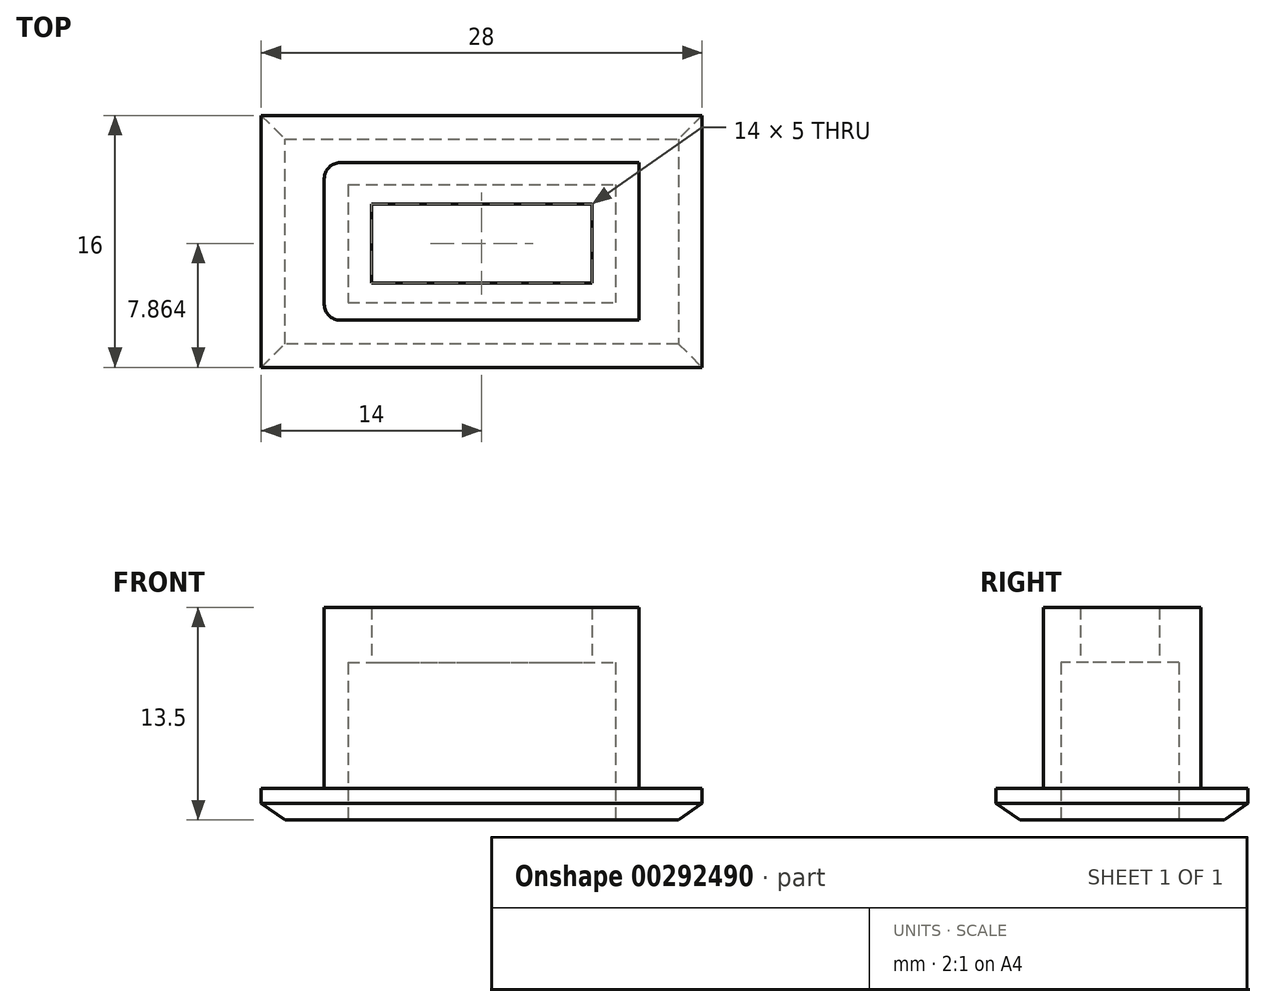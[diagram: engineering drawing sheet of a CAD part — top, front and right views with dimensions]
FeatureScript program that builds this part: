
annotation { "Feature Type Name" : "Feature", "Feature Type Description" : "" }
export const myFeature = defineFeature(function(context is Context, id is Id, definition is map)
    precondition{}
    {
        {
            var Q0;
            Q0=qCreatedBy(makeId("Front.planeOp"),FACE);
            var sketch = newSketch(context, id + "F0", { "sketchPlane" : qUnion([Q0])});
            skLineSegment(sketch, "E0.bottom", {"start": v(10, 5.75) * mm, "end": v(-10, 5.75) * mm});
            skLineSegment(sketch, "E0.top", {"start": v(10, -5.75) * mm, "end": v(-10, -5.75) * mm});
            skLineSegment(sketch, "E0.left", {"start": v(10, 5.75) * mm, "end": v(10, -5.75) * mm});
            skLineSegment(sketch, "E0.right", {"start": v(-10, 5.75) * mm, "end": v(-10, -5.75) * mm});
            skPoint(sketch, "E0.middle", {"position": v(0, 0) * mm});
            skLineSegment(sketch, "E1.bottom", {"start": v(-14, -5.75) * mm, "end": v(14, -5.75) * mm});
            skLineSegment(sketch, "E1.top", {"start": v(-14, -7.75) * mm, "end": v(14, -7.75) * mm});
            skLineSegment(sketch, "E1.left", {"start": v(-14, -5.75) * mm, "end": v(-14, -7.75) * mm});
            skLineSegment(sketch, "E1.right", {"start": v(14, -5.75) * mm, "end": v(14, -7.75) * mm});
            skSolve(sketch);
        }
        {
            var Q0;
            Q0=makeQuery(id+"F0.imprint","IMPRINT",FACE,{"disambiguationData":[TD([[makeQuery(id+"F0.imprint","IMPRINT",EDGE,{"derivedFrom":sQuery(id+"F0.wireOp",EDGE,"E0.bottom")}),1.0]])]});
            var Q1;
            Q1=makeQuery(id+"F0.imprint","IMPRINT",FACE,{"disambiguationData":[TD([[makeQuery(id+"F0.imprint","IMPRINT",EDGE,{"derivedFrom":sQuery(id+"F0.wireOp",EDGE,"E1.top")}),1.0]])]});
            extrude(context, id + "F1", {"entities" : qUnion([Q0, Q1]), "oppositeDirection" : true, "depth" : 16 * mm});
        }
        {
            var Q0;
            Q0=makeQuery(id+"F1.opExtrude","SWEPT_FACE",FACE,{"disambiguationData":[OSD([sQuery(id+"F0.wireOp",EDGE,"E0.left")])]});
            var sketch = newSketch(context, id + "F2", { "sketchPlane" : qUnion([Q0])});
            skLineSegment(sketch, "E2", {"start": v(8, 9.28) * mm, "end": v(8, -10.72) * mm, "construction": true});
            skLineSegment(sketch, "E3.bottom", {"start": v(0, 5.75) * mm, "end": v(3, 5.75) * mm});
            skLineSegment(sketch, "E3.top", {"start": v(0, -5.75) * mm, "end": v(3, -5.75) * mm});
            skLineSegment(sketch, "E3.left", {"start": v(0, 5.75) * mm, "end": v(0, -5.75) * mm});
            skLineSegment(sketch, "E3.right", {"start": v(3, 5.75) * mm, "end": v(3, -5.75) * mm});
            skLineSegment(sketch, "E4.MirrorCS", {"start": v(13, 5.75) * mm, "end": v(13, -5.75) * mm});
            skLineSegment(sketch, "E5.MirrorCS", {"start": v(16, 5.75) * mm, "end": v(13, 5.75) * mm});
            skLineSegment(sketch, "E6.MirrorCS", {"start": v(16, 5.75) * mm, "end": v(16, -5.75) * mm});
            skLineSegment(sketch, "E7.MirrorCS", {"start": v(16, -5.75) * mm, "end": v(13, -5.75) * mm});
            skSolve(sketch);
        }
        {
            var Q0;
            Q0=makeQuery(id+"F2.imprint","IMPRINT",FACE,{"disambiguationData":[TD([[makeQuery(id+"F2.imprint","IMPRINT",EDGE,{"derivedFrom":sQuery(id+"F2.wireOp",EDGE,"E3.bottom")}),1.0]])]});
            var Q1;
            Q1=makeQuery(id+"F2.imprint","IMPRINT",FACE,{"disambiguationData":[TD([[makeQuery(id+"F2.imprint","IMPRINT",EDGE,{"derivedFrom":sQuery(id+"F2.wireOp",EDGE,"E4.MirrorCS")}),1.0]])]});
            extrude(context, id + "F3", {"entities" : qUnion([Q0, Q1]), "operationType" : NewBodyOperationType.REMOVE, "oppositeDirection" : true, "depth" : 25 * mm});
        }
        {
            var Q0;
            Q0=makeQuery(id+"F1.opExtrude","SWEPT_FACE",FACE,{"disambiguationData":[OSD([sQuery(id+"F0.wireOp",EDGE,"E1.top")])]});
            var sketch = newSketch(context, id + "F4", { "sketchPlane" : qUnion([Q0])});
            skLineSegment(sketch, "E8", {"start": v(17.54, -7.86) * mm, "end": v(-16.5, -7.86) * mm, "construction": true});
            skLineSegment(sketch, "E9.bottom", {"start": v(-8.5, -11.61) * mm, "end": v(8.5, -11.61) * mm});
            skLineSegment(sketch, "E9.top", {"start": v(-8.5, -4.11) * mm, "end": v(8.5, -4.11) * mm});
            skLineSegment(sketch, "E9.left", {"start": v(-8.5, -11.61) * mm, "end": v(-8.5, -4.11) * mm});
            skLineSegment(sketch, "E9.right", {"start": v(8.5, -11.61) * mm, "end": v(8.5, -4.11) * mm});
            skPoint(sketch, "E9.middle", {"position": v(0, -7.86) * mm});
            skLineSegment(sketch, "E10.bottom", {"start": v(-7, -10.36) * mm, "end": v(7, -10.36) * mm});
            skLineSegment(sketch, "E10.top", {"start": v(-7, -5.36) * mm, "end": v(7, -5.36) * mm});
            skLineSegment(sketch, "E10.left", {"start": v(-7, -10.36) * mm, "end": v(-7, -5.36) * mm});
            skLineSegment(sketch, "E10.right", {"start": v(7, -10.36) * mm, "end": v(7, -5.36) * mm});
            skSolve(sketch);
        }
        {
            var Q0;
            Q0=makeQuery(id+"F4.imprint","IMPRINT",FACE,{"disambiguationData":[TD([[makeQuery(id+"F4.imprint","IMPRINT",EDGE,{"derivedFrom":sQuery(id+"F4.wireOp",EDGE,"E9.bottom")}),1.0]])]});
            extrude(context, id + "F5", {"entities" : qUnion([Q0]), "operationType" : NewBodyOperationType.REMOVE, "oppositeDirection" : true, "depth" : 10 * mm});
        }
        {
            var Q0;
            Q0=makeQuery(id+"F4.imprint","IMPRINT",FACE,{"disambiguationData":[TD([[makeQuery(id+"F4.imprint","IMPRINT",EDGE,{"derivedFrom":sQuery(id+"F4.wireOp",EDGE,"E10.bottom")}),1.0]])]});
            extrude(context, id + "F6", {"entities" : qUnion([Q0]), "operationType" : NewBodyOperationType.REMOVE, "oppositeDirection" : true, "depth" : 25 * mm});
        }
        {
            var Q0;
            Q0=makeQuery(id+"F1.opExtrude","CAP_EDGE",EDGE,{"disambiguationData":[OSD([sQuery(id+"F0.wireOp",EDGE,"E1.top")])],"isStart":false});
            var Q1;
            Q1=makeQuery(id+"F1.opExtrude","SWEPT_EDGE",EDGE,{"disambiguationData":[OSD([sQuery(id+"F0.wireOp",EDGE,"E1.top"),sQuery(id+"F0.wireOp",EDGE,"E1.right")])]});
            var Q2;
            Q2=makeQuery(id+"F1.opExtrude","CAP_EDGE",EDGE,{"disambiguationData":[OSD([sQuery(id+"F0.wireOp",EDGE,"E1.top")])],"isStart":true});
            var Q3;
            Q3=makeQuery(id+"F1.opExtrude","SWEPT_EDGE",EDGE,{"disambiguationData":[OSD([sQuery(id+"F0.wireOp",EDGE,"E1.top"),sQuery(id+"F0.wireOp",EDGE,"E1.left")])]});
            chamfer(context, id + "F7", {"entities" : qUnion([Q0, Q1, Q2, Q3]), "chamferType" : ChamferType.OFFSET_ANGLE, "width" : 1.5 * mm, "oppositeDirection" : false, "angle" : 35 * degree, "tangentPropagation" : true});
        }
        {
            var Q0;
            Q0=makeQuery(id+"F3.boolean.opBoolean","COPY",EDGE,{"derivedFrom":makeQuery(id+"F3.opExtrude","CAP_EDGE",EDGE,{"disambiguationData":[OSD([sQuery(id+"F2.wireOp",EDGE,"E3.right")])],"isStart":true})});
            var Q1;
            Q1=makeQuery(id+"F3.boolean.opBoolean","COPY",EDGE,{"derivedFrom":makeQuery(id+"F3.opExtrude","CAP_EDGE",EDGE,{"disambiguationData":[OSD([sQuery(id+"F2.wireOp",EDGE,"E4.MirrorCS")])],"isStart":true})});
            var Q2;
            Q2=makeQuery(id+"F3.boolean.opBoolean","INTERSECT",EDGE,{"derivedFrom":[makeQuery(id+"F1.opExtrude","SWEPT_FACE",FACE,{"disambiguationData":[OSD([sQuery(id+"F0.wireOp",EDGE,"E0.right")])]}),makeQuery(id+"F3.opExtrude","SWEPT_FACE",FACE,{"disambiguationData":[OSD([sQuery(id+"F2.wireOp",EDGE,"E3.right")])]})]});
            var Q3;
            Q3=makeQuery(id+"F3.boolean.opBoolean","INTERSECT",EDGE,{"derivedFrom":[makeQuery(id+"F1.opExtrude","SWEPT_FACE",FACE,{"disambiguationData":[OSD([sQuery(id+"F0.wireOp",EDGE,"E0.right")])]}),makeQuery(id+"F3.opExtrude","SWEPT_FACE",FACE,{"disambiguationData":[OSD([sQuery(id+"F2.wireOp",EDGE,"E4.MirrorCS")])]})]});
            fillet(context, id + "F8", {"entities" : qUnion([Q0, Q1, Q2, Q3]), "radius" : 1 * mm, "tangentPropagation" : true, "allowEdgeOverflow" : false});
        }
    });
